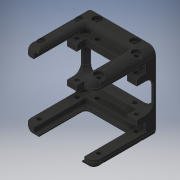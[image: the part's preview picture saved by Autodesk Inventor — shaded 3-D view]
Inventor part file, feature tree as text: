
AUTODESK INVENTOR PART (.ipt)
format: ipt  version: 2019 (Build 230136000, 136)  size: 571,392 bytes
history: native  units: mm
features: extrude x10, sketch x5, mirror x5, fillet x3, plane x1, chamfer x1, projected_geometry x1
ambient origin geometry x8: Origin, YZ Plane, XZ Plane, XY Plane, X Axis, Y Axis, Z Axis, Center Point
bodies: Solid1 (feature_tree)
feature tree (26):
  plane  "Work Plane1"
  sketch  "Sketch2"  dims[d2=38.0mm d3=29.5mm]
  extrude  "Extrusion1"  Depth=29.5mm
  extrude  "Extrusion2"  Depth=25.0mm
  extrude  "Extrusion3"  Depth=36.0mm TaperAngle=0.0deg
  mirror  "Mirror2"
  sketch  "Sketch5"  dims[d10=17.25mm d11=5.6mm d12=2.0mm]
  mirror  "Mirror1"
  fillet  "Fillet1"  Radius=5.6mm
  extrude  "Extrusion4"  Depth=5.6mm
  fillet  "Fillet2"  Radius=2.0mm
  extrude  "Extrusion5"  Depth=4.0mm
  extrude  "Extrusion9"  Depth=4.0mm TaperAngle=0.0deg
  extrude  "Extrusion10"  Depth=4.0mm
  chamfer  "Chamfer2"  Distance=9.773844mm
  mirror  "Mirror3"
  extrude  "Extrusion6"  Depth=4.0mm TaperAngle=0.0deg
  extrude  "Extrusion7"  Depth=4.0mm
  mirror  "Mirror4"
  mirror  "Mirror5"
  extrude  "Extrusion8"  Depth=4.0mm
  fillet  "Fillet3"  Radius=4.0mm
  sketch  "Sketch3"  dims[d4=41.5mm d5=25.0mm]
  sketch  "Sketch4"  dims[d6=29.5mm d7=36.0mm d8=0.0mm d9=5.6mm]
  sketch  "Sketch7"  dims[d13=5.6mm d14=0.0mm d15=4.0mm d17=5.6mm d18=0.0mm d27=5.0mm d28=9.773844mm d32=5.6mm d33=0.0mm d34=3.75mm d35=0.5mm d36=4.0mm d37=5.6mm d38=0.0mm d39=8.1mm d40=34.6mm d41=2.7mm d42=22.0mm d43=30.1mm d44=2.5mm d45=5.0mm d46=2.5mm d47=5.0mm d48=2.5mm d49=5.0mm d50=10.0mm d51=0.0mm d52=2.0mm d53=0.0mm d60=2.0mm d61=2.0mm d62=2.0mm d63=0.0mm d64=4.0mm d65=0.5mm d71=11.0mm d72=0.0mm d73=4.0mm d74=4.0mm d75=3.0mm d76=0.0mm d80=1.0mm d81=2.0mm d82=45.0deg d83=2.0mm d84=2.0mm d85=2.0mm]
  projected_geometry  "Projected Loop1"
